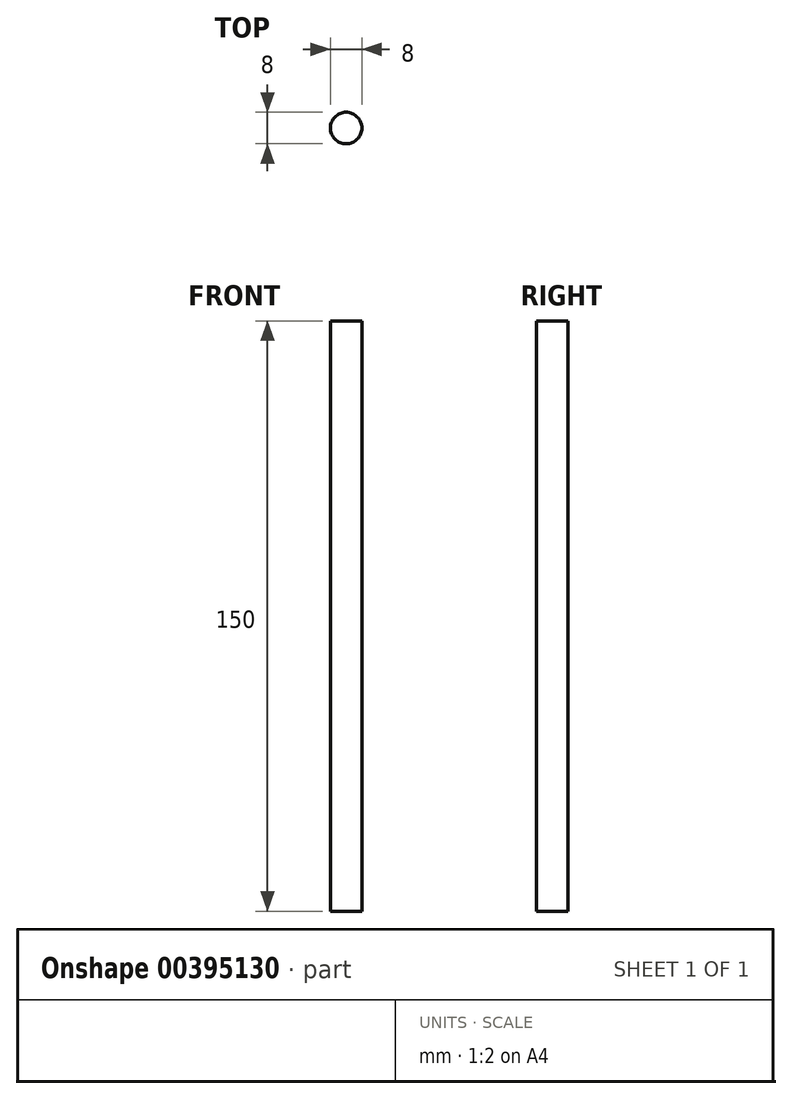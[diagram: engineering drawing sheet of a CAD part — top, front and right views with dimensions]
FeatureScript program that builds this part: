
annotation { "Feature Type Name" : "Feature", "Feature Type Description" : "" }
export const myFeature = defineFeature(function(context is Context, id is Id, definition is map)
    precondition{}
    {
        {
            var Q0;
            Q0=qCreatedBy(makeId("Top.planeOp"),FACE);
            var sketch = newSketch(context, id + "F0", { "sketchPlane" : qUnion([Q0])});
            skCircle(sketch, "E0", {"center": v(0, 0) * mm, "radius": 4 * mm});
            skSolve(sketch);
        }
        {
            var Q0;
            Q0=qSketchRegion(id+"F0",true);
            extrude(context, id + "F1", {"entities" : qUnion([Q0]), "endBound" : BoundingType.SYMMETRIC, "depth" : 150 * mm});
        }
    });
